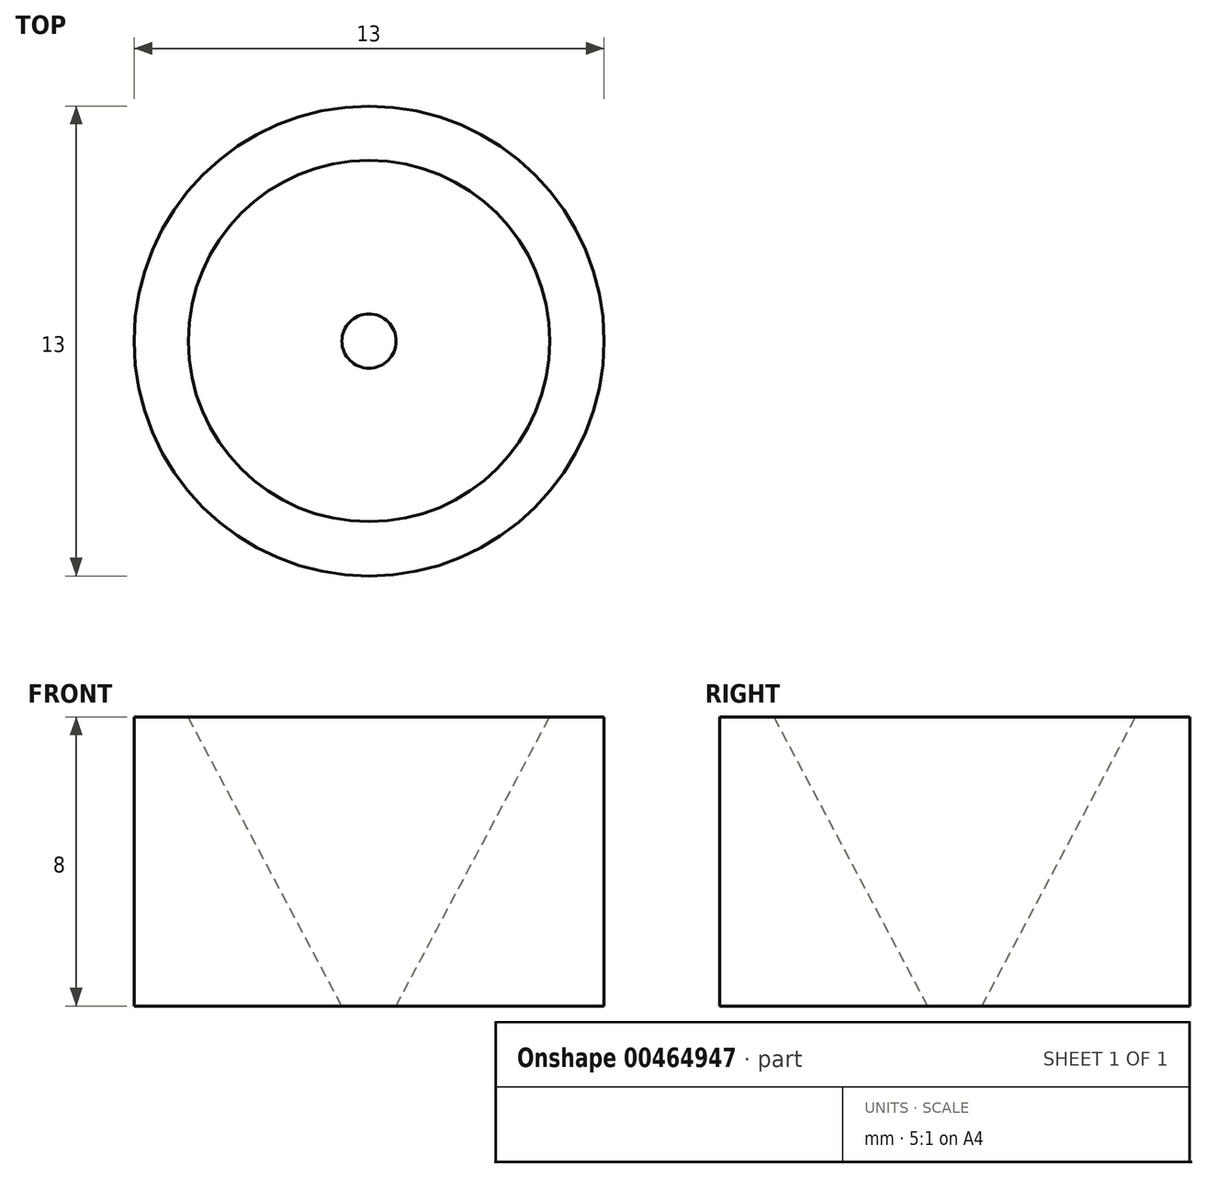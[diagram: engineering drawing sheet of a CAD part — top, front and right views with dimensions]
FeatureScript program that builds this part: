
annotation { "Feature Type Name" : "Feature", "Feature Type Description" : "" }
export const myFeature = defineFeature(function(context is Context, id is Id, definition is map)
    precondition{}
    {
        {
            var Q0;
            Q0=qCreatedBy(makeId("Top.planeOp"),FACE);
            var sketch = newSketch(context, id + "F0", { "sketchPlane" : qUnion([Q0])});
            skCircle(sketch, "E0", {"center": v(0, 0) * mm, "radius": 6.5 * mm});
            skSolve(sketch);
        }
        {
            var Q0;
            Q0=qSketchRegion(id+"F0",true);
            extrude(context, id + "F1", {"entities" : qUnion([Q0]), "depth" : 8 * mm});
        }
        {
            var Q0;
            Q0=makeQuery(id+"F1.opExtrude","CAP_FACE",FACE,{"disambiguationData":[OSD([sQuery(id+"F0.wireOp",EDGE,"E0")])],"isStart":true});
            var sketch = newSketch(context, id + "F2", { "sketchPlane" : qUnion([Q0])});
            skCircle(sketch, "E1", {"center": v(0, 0) * mm, "radius": 0.75 * mm});
            skSolve(sketch);
        }
        {
            var Q0;
            Q0=makeQuery(id+"F1.opExtrude","CAP_FACE",FACE,{"disambiguationData":[OSD([sQuery(id+"F0.wireOp",EDGE,"E0")])],"isStart":false});
            var sketch = newSketch(context, id + "F3", { "sketchPlane" : qUnion([Q0])});
            skCircle(sketch, "E2", {"center": v(0, 0) * mm, "radius": 5 * mm});
            skSolve(sketch);
        }
        {
            var Q1;
            Q1=makeQuery(id+"F2.imprint","IMPRINT",FACE,{"disambiguationData":[TD([[makeQuery(id+"F2.imprint","IMPRINT",EDGE,{"derivedFrom":sQuery(id+"F2.wireOp",EDGE,"E1")}),1.0]])]});
            var Q2;
            Q2=makeQuery(id+"F3.imprint","IMPRINT",FACE,{"disambiguationData":[TD([[makeQuery(id+"F3.imprint","IMPRINT",EDGE,{"derivedFrom":sQuery(id+"F3.wireOp",EDGE,"E2")}),1.0]])]});
            loft(context, id + "F4", {"operationType" : NewBodyOperationType.REMOVE, "sheetProfilesArray" : [{ "sheetProfileEntities" : qUnion([Q1]) }, { "sheetProfileEntities" : qUnion([Q2]) }]});
        }
    });
